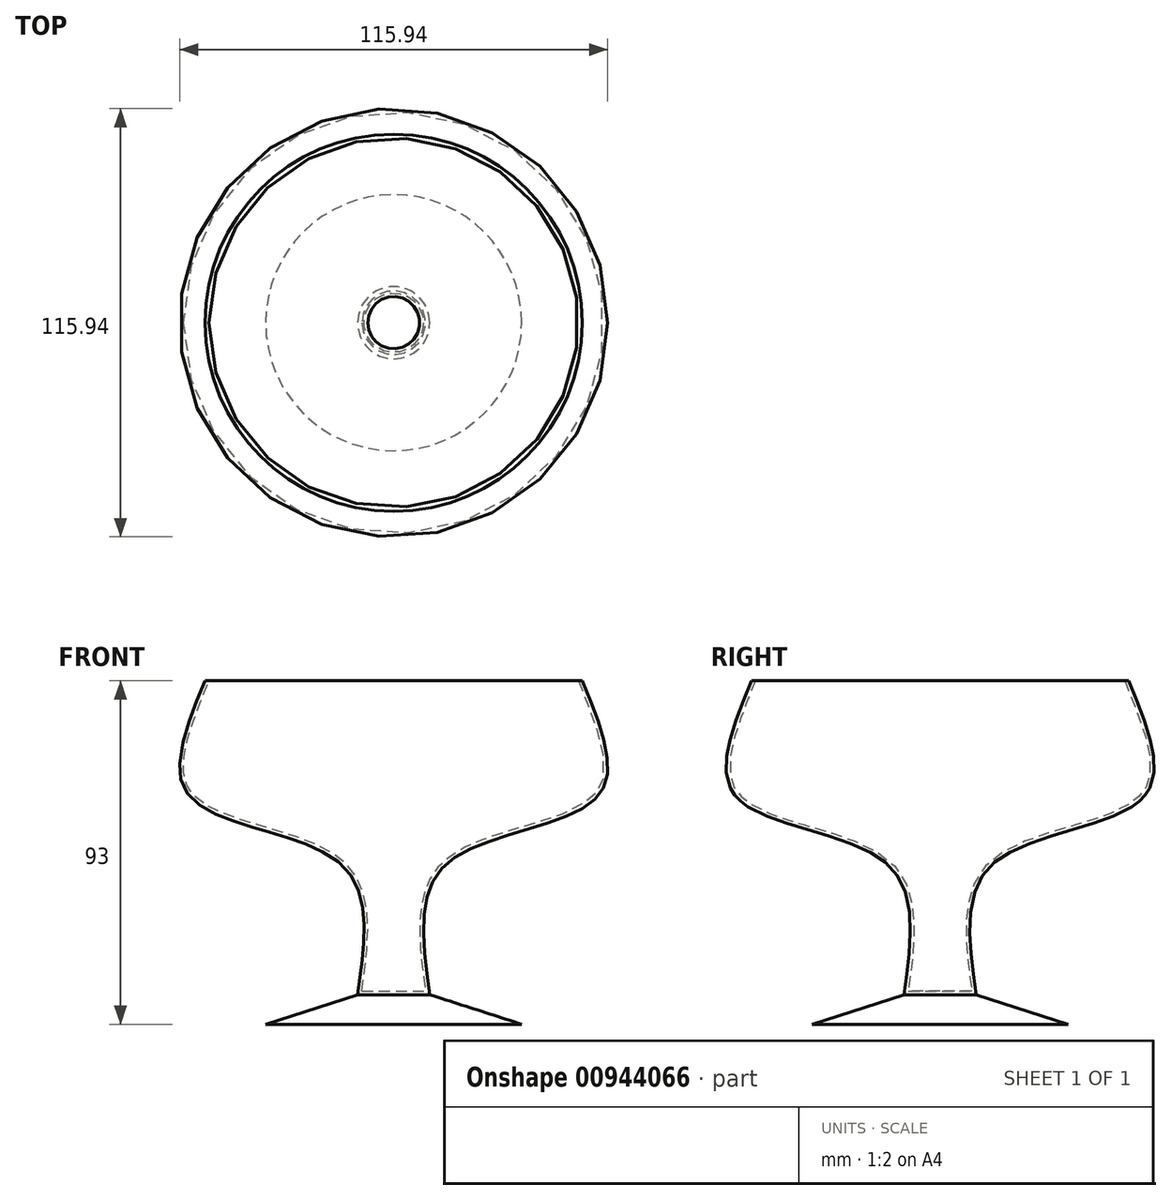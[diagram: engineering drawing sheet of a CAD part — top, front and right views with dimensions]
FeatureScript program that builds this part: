
annotation { "Feature Type Name" : "Feature", "Feature Type Description" : "" }
export const myFeature = defineFeature(function(context is Context, id is Id, definition is map)
    precondition{}
    {
        {
            var Q0;
            Q0=qCreatedBy(makeId("Top.planeOp"),FACE);
            var sketch = newSketch(context, id + "F0", { "sketchPlane" : qUnion([Q0])});
            skCircle(sketch, "E0", {"center": v(0, 0) * mm, "radius": 9.76 * mm});
            skSolve(sketch);
        }
        {
            var Q0;
            Q0=qCreatedBy(makeId("Top.planeOp"),FACE);
            cPlane(context, id + "F1", {"entities" : qUnion([Q0]), "cplaneType" : CPlaneType.OFFSET, "offset" : 85 * mm, "width" : 152.4 * mm, "height" : 152.4 * mm});
        }
        {
            var Q0;
            Q0=qCreatedBy(id+"F1.planeOp",FACE);
            var sketch = newSketch(context, id + "F2", { "sketchPlane" : qUnion([Q0])});
            skCircle(sketch, "E1", {"center": v(0, 0) * mm, "radius": 51.07 * mm});
            skSolve(sketch);
        }
        {
            var Q0;
            Q0=qCreatedBy(makeId("Top.planeOp"),FACE);
            cPlane(context, id + "F3", {"entities" : qUnion([Q0]), "cplaneType" : CPlaneType.OFFSET, "offset" : 34.2 * mm, "width" : 150 * mm, "height" : 150 * mm});
        }
        {
            var Q0;
            Q0=qCreatedBy(makeId("Top.planeOp"),FACE);
            cPlane(context, id + "F4", {"entities" : qUnion([Q0]), "cplaneType" : CPlaneType.OFFSET, "offset" : 55.7 * mm, "width" : 150 * mm, "height" : 150 * mm});
        }
        {
            var Q0;
            Q0=qCreatedBy(id+"F3.planeOp",FACE);
            var sketch = newSketch(context, id + "F5", { "sketchPlane" : qUnion([Q0])});
            skCircle(sketch, "E2", {"center": v(0, 0) * mm, "radius": 13.06 * mm});
            skSolve(sketch);
        }
        {
            var Q0;
            Q0=qCreatedBy(id+"F4.planeOp",FACE);
            var sketch = newSketch(context, id + "F6", { "sketchPlane" : qUnion([Q0])});
            skCircle(sketch, "E3", {"center": v(0, 0) * mm, "radius": 56.67 * mm});
            skSolve(sketch);
        }
        {
            var Q0;
            Q0=makeQuery(id+"F0.imprint","IMPRINT",FACE,{"disambiguationData":[TD([[makeQuery(id+"F0.imprint","IMPRINT",EDGE,{"derivedFrom":sQuery(id+"F0.wireOp",EDGE,"E0")}),1.0]])]});
            var Q1;
            Q1=makeQuery(id+"F5.imprint","IMPRINT",FACE,{"disambiguationData":[TD([[makeQuery(id+"F5.imprint","IMPRINT",EDGE,{"derivedFrom":sQuery(id+"F5.wireOp",EDGE,"E2")}),1.0]])]});
            var Q2;
            Q2=makeQuery(id+"F6.imprint","IMPRINT",FACE,{"disambiguationData":[TD([[makeQuery(id+"F6.imprint","IMPRINT",EDGE,{"derivedFrom":sQuery(id+"F6.wireOp",EDGE,"E3")}),1.0]])]});
            var Q3;
            Q3=makeQuery(id+"F2.imprint","IMPRINT",FACE,{"disambiguationData":[TD([[makeQuery(id+"F2.imprint","IMPRINT",EDGE,{"derivedFrom":sQuery(id+"F2.wireOp",EDGE,"E1")}),1.0]])]});
            loft(context, id + "F7", {"sheetProfilesArray" : [{ "sheetProfileEntities" : qUnion([Q0]) }, { "sheetProfileEntities" : qUnion([Q1]) }, { "sheetProfileEntities" : qUnion([Q2]) }, { "sheetProfileEntities" : qUnion([Q3]) }]});
        }
        {
            var Q0;
            Q0=makeQuery(id+"F7.opLoft","CAP_FACE",FACE,{"disambiguationData":[OSD([makeQuery(id+"F2.imprint","IMPRINT",FACE,{"disambiguationData":[TD([[makeQuery(id+"F2.imprint","IMPRINT",EDGE,{"derivedFrom":sQuery(id+"F2.wireOp",EDGE,"E1")}),1.0]])]})])],"isStart":true});
            shell(context, id + "F8", {"entities" : qUnion([Q0]), "thickness" : 1 * mm});
        }
        {
            var Q0;
            Q0=qCreatedBy(makeId("Top.planeOp"),FACE);
            cPlane(context, id + "F9", {"entities" : qUnion([Q0]), "cplaneType" : CPlaneType.OFFSET, "offset" : 8 * mm, "oppositeDirection" : true, "width" : 150 * mm, "height" : 150 * mm});
        }
        {
            var Q0;
            Q0=qCreatedBy(id+"F9.planeOp",FACE);
            var sketch = newSketch(context, id + "F10", { "sketchPlane" : qUnion([Q0])});
            skCircle(sketch, "E4", {"center": v(0, 0) * mm, "radius": 34.67 * mm});
            skSolve(sketch);
        }
        {
            var Q1;
            Q1=makeQuery(id+"F7.opLoft","CAP_FACE",FACE,{"disambiguationData":[OSD([makeQuery(id+"F0.imprint","IMPRINT",FACE,{"disambiguationData":[TD([[makeQuery(id+"F0.imprint","IMPRINT",EDGE,{"derivedFrom":sQuery(id+"F0.wireOp",EDGE,"E0")}),1.0]])]})])],"isStart":true});
            var Q2;
            Q2=makeQuery(id+"F10.imprint","IMPRINT",FACE,{"disambiguationData":[TD([[makeQuery(id+"F10.imprint","IMPRINT",EDGE,{"derivedFrom":sQuery(id+"F10.wireOp",EDGE,"E4")}),1.0]])]});
            loft(context, id + "F11", {"operationType" : NewBodyOperationType.ADD, "sheetProfilesArray" : [{ "sheetProfileEntities" : qUnion([Q1]) }, { "sheetProfileEntities" : qUnion([Q2]) }]});
        }
    });
